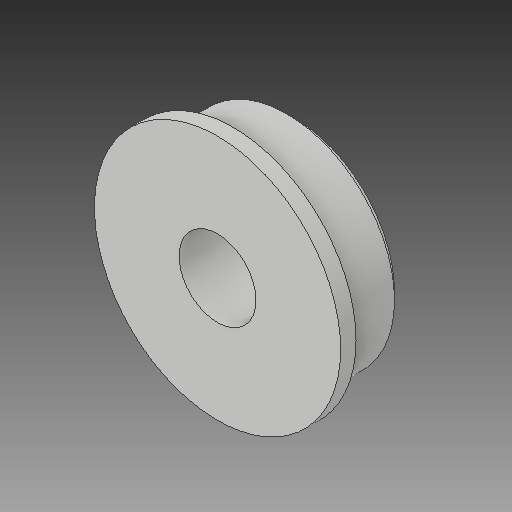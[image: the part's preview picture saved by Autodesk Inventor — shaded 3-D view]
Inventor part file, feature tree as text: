
AUTODESK INVENTOR PART (.ipt)
format: ipt  version: 2018 (Build 220112000, 112)  size: 122,368 bytes
history: native  units: mm
features: other x3, extrude x2, sketch x2, chamfer x1, reference x1
ambient origin geometry x8: Origin, YZ Plane, XZ Plane, XY Plane, X Axis, Y Axis, Z Axis, Center Point
bodies: Solid1 (feature_tree)
feature tree (9):
  extrude  "Extrusion1"  Depth=5.0mm
  extrude  "Extrusion2"  Depth=1.0mm
  chamfer  "Chamfer1"  Distance=1.0mm
  sketch  "Sketch1"  dims[d0=5.0mm d1=14.0mm]
  reference  "Reference1"
  sketch  "Sketch2"  dims[d2=5.0mm d3=0.0mm d4=16.0mm d5=1.0mm d6=0.0mm d7=0.5mm d8=2.0mm d9=45.0deg]
  other  "<userpath>\OneDrive\SL-Inventor\SL-Beast 3D Printer\x-aXIS-aSSEMBLY.iam"
  other  "x-aXIS-aSSEMBLY.iam"
  other  "Washer:1"
